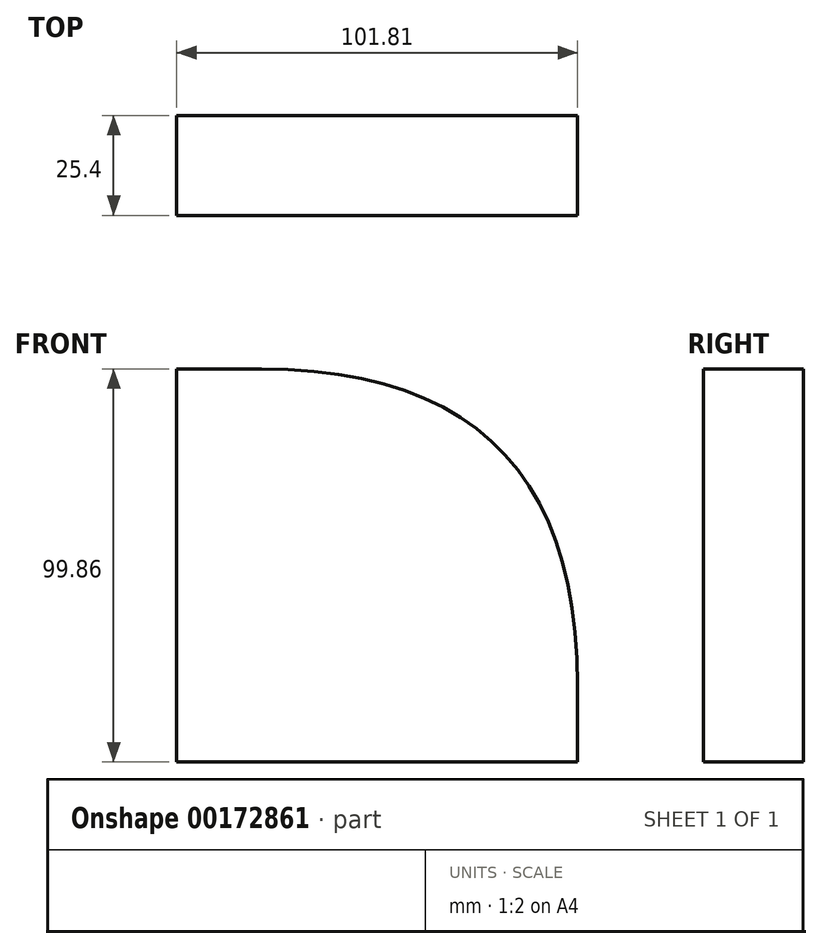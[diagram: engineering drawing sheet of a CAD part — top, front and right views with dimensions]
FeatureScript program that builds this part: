
annotation { "Feature Type Name" : "Feature", "Feature Type Description" : "" }
export const myFeature = defineFeature(function(context is Context, id is Id, definition is map)
    precondition{}
    {
        {
            var Q0;
            Q0=qCreatedBy(makeId("Front.planeOp"),FACE);
            var sketch = newSketch(context, id + "F0", { "sketchPlane" : qUnion([Q0])});
            skLineSegment(sketch, "E0.bottom", {"start": v(-53.1, 44.45) * mm, "end": v(48.71, 44.45) * mm});
            skLineSegment(sketch, "E0.top", {"start": v(-53.1, -55.41) * mm, "end": v(48.71, -55.41) * mm});
            skLineSegment(sketch, "E0.left", {"start": v(-53.1, 44.45) * mm, "end": v(-53.1, -55.41) * mm});
            skLineSegment(sketch, "E0.right", {"start": v(48.71, 44.45) * mm, "end": v(48.71, -55.41) * mm});
            skSolve(sketch);
        }
        {
            var Q0;
            Q0=makeQuery(id+"F0.imprint","IMPRINT",FACE,{"disambiguationData":[TD([[makeQuery(id+"F0.imprint","IMPRINT",EDGE,{"derivedFrom":sQuery(id+"F0.wireOp",EDGE,"E0.bottom")}),-1.0]])]});
            extrude(context, id + "F1", {"entities" : qUnion([Q0]), "depth" : 25.4 * mm});
        }
        {
            var Q0;
            Q0=makeQuery(id+"F1.opExtrude","SWEPT_EDGE",EDGE,{"disambiguationData":[OSD([sQuery(id+"F0.wireOp",EDGE,"E0.bottom"),sQuery(id+"F0.wireOp",EDGE,"E0.right")])]});
            fillet(context, id + "F2", {"entities" : qUnion([Q0]), "radius" : 80.33 * mm, "tangentPropagation" : true, "rho" : 0.5, "crossSection" : FilletCrossSection.CONIC, "allowEdgeOverflow" : false});
        }
    });
